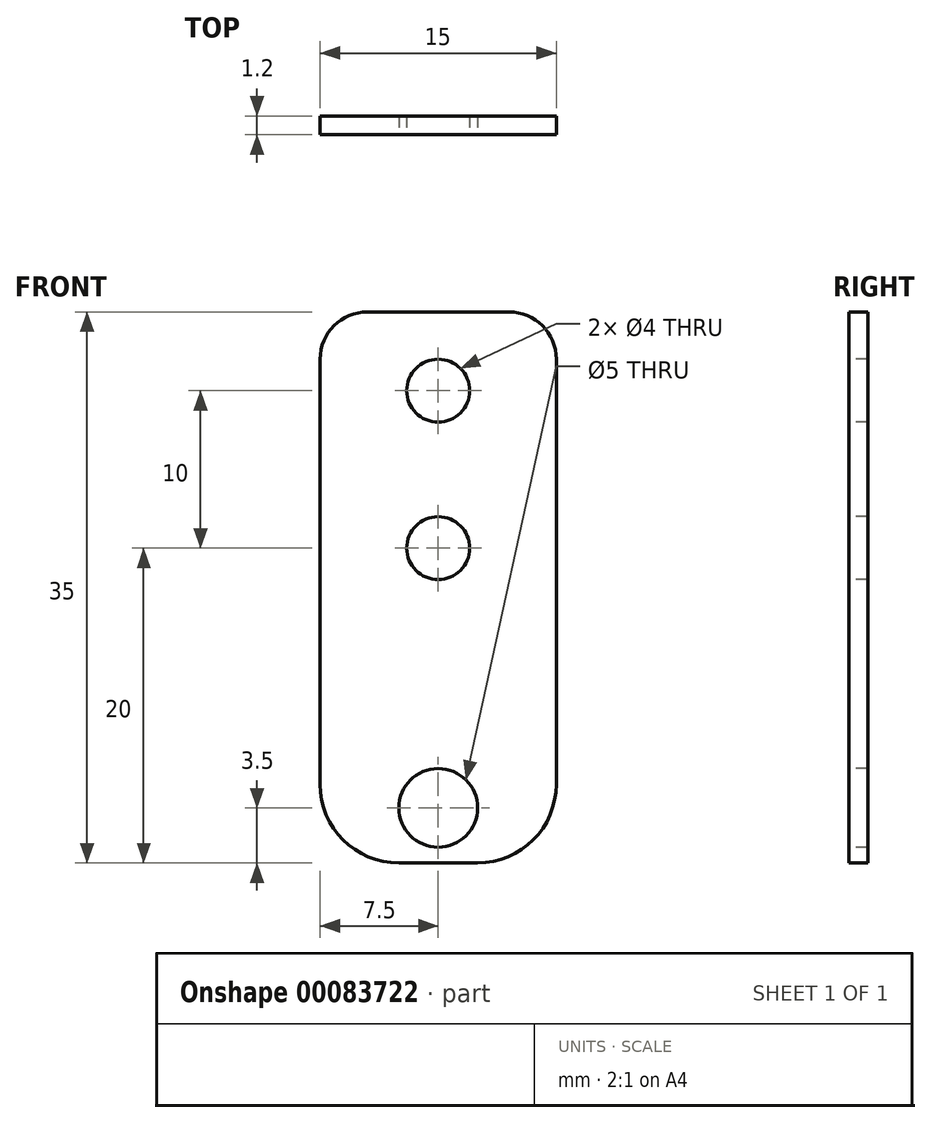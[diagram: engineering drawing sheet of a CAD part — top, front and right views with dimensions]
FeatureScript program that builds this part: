
annotation { "Feature Type Name" : "Feature", "Feature Type Description" : "" }
export const myFeature = defineFeature(function(context is Context, id is Id, definition is map)
    precondition{}
    {
        {
            var Q0;
            Q0=qCreatedBy(makeId("Front.planeOp"),FACE);
            var sketch = newSketch(context, id + "F0", { "sketchPlane" : qUnion([Q0])});
            skLineSegment(sketch, "E0.rect.bottom", {"start": v(2.5, -17.5) * mm, "end": v(-2.5, -17.5) * mm});
            skLineSegment(sketch, "E0.rect.top", {"start": v(4.5, 17.5) * mm, "end": v(-4.5, 17.5) * mm});
            skLineSegment(sketch, "E0.rect.left", {"start": v(7.5, -12.5) * mm, "end": v(7.5, 14.5) * mm});
            skLineSegment(sketch, "E0.rect.right", {"start": v(-7.5, -12.5) * mm, "end": v(-7.5, 14.5) * mm});
            skPoint(sketch, "E0.rect.middle", {"position": v(0, 0) * mm});
            skPoint(sketch, "E1.visualSharp", {"position": v(-7.5, 17.5) * mm});
            skArc(sketch, "E1.filletArc", {"start": v(-4.5, 17.5) * mm, "mid": v(-6.62, 16.62) * mm, "end": v(-7.5, 14.5) * mm});
            skPoint(sketch, "E2.visualSharp", {"position": v(7.5, 17.5) * mm});
            skArc(sketch, "E2.filletArc", {"start": v(7.5, 14.5) * mm, "mid": v(6.62, 16.62) * mm, "end": v(4.5, 17.5) * mm});
            skPoint(sketch, "E3.visualSharp", {"position": v(-7.5, -17.5) * mm});
            skPoint(sketch, "E4.visualSharp", {"position": v(7.5, -17.5) * mm});
            skCircle(sketch, "E5", {"center": v(0, 12.5) * mm, "radius": 2 * mm});
            skCircle(sketch, "E6", {"center": v(0, 2.5) * mm, "radius": 2 * mm});
            skCircle(sketch, "E7", {"center": v(0, -14) * mm, "radius": 2.5 * mm});
            skLineSegment(sketch, "E8", {"start": v(0, 17.5) * mm, "end": v(0, -18.5) * mm, "construction": true});
            skPoint(sketch, "E8.endSnap0", {"position": v(0, -17.5) * mm});
            skArc(sketch, "E9.filletArc", {"start": v(-7.5, -12.5) * mm, "mid": v(-6.04, -16.04) * mm, "end": v(-2.5, -17.5) * mm});
            skArc(sketch, "E10.filletArc", {"start": v(2.5, -17.5) * mm, "mid": v(6.04, -16.04) * mm, "end": v(7.5, -12.5) * mm});
            skSolve(sketch);
        }
        {
            var Q0;
            Q0=qSketchRegion(id+"F0",true);
            extrude(context, id + "F1", {"entities" : qUnion([Q0]), "oppositeDirection" : true, "depth" : 1.2 * mm});
        }
    });
